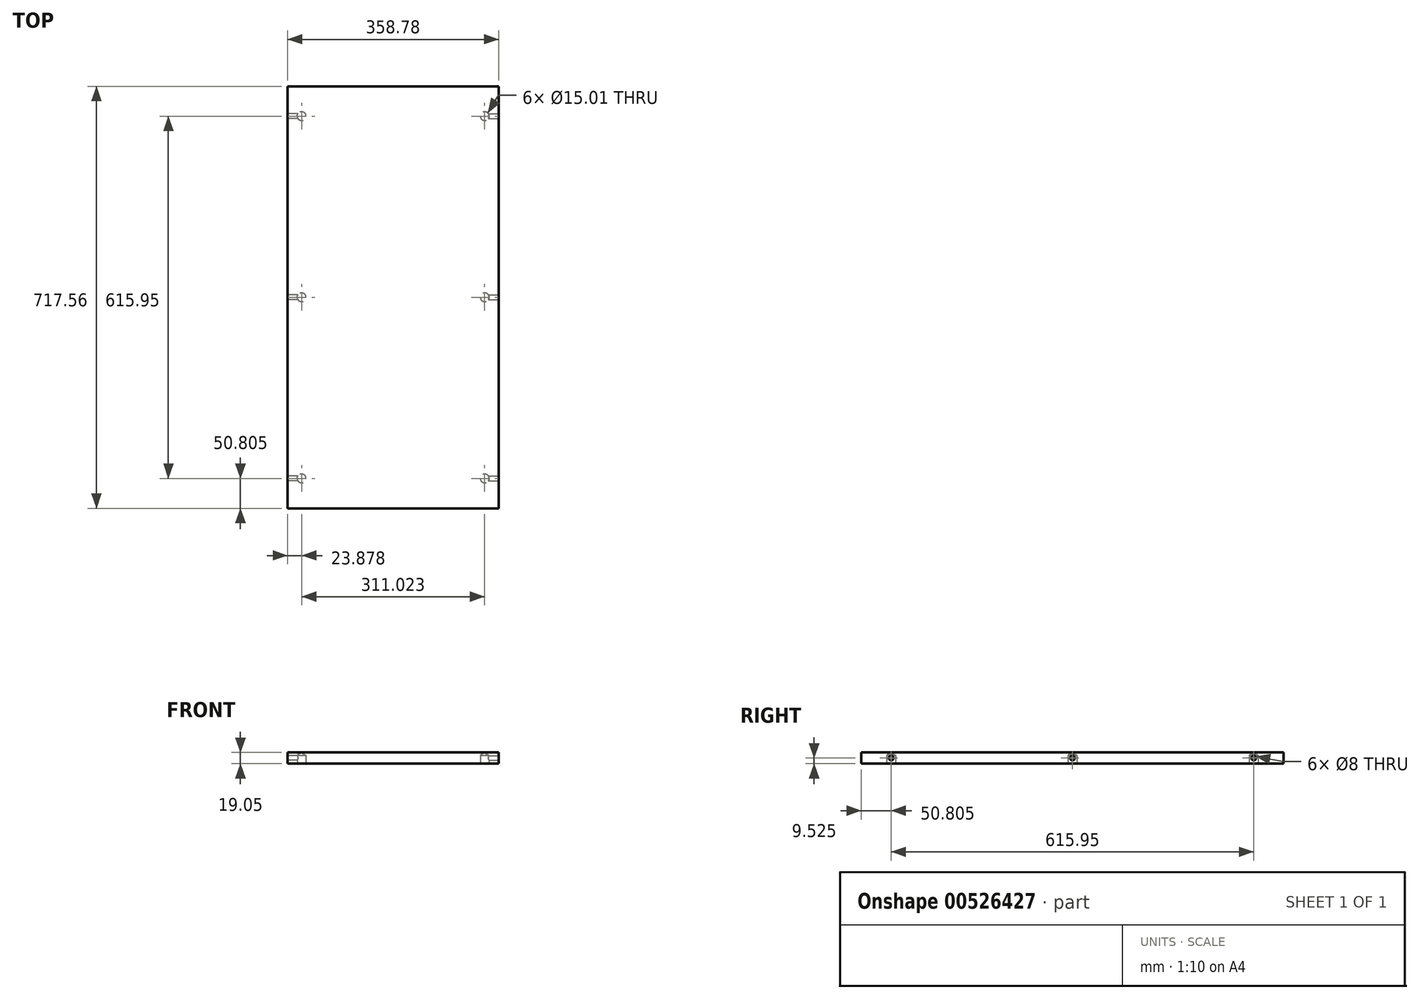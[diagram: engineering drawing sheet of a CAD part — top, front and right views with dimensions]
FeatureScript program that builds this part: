
annotation { "Feature Type Name" : "Feature", "Feature Type Description" : "" }
export const myFeature = defineFeature(function(context is Context, id is Id, definition is map)
    precondition{}
    {
        {
            var Q0;
            Q0=qCreatedBy(makeId("Top.planeOp"),FACE);
            var sketch = newSketch(context, id + "F0", { "sketchPlane" : qUnion([Q0])});
            skLineSegment(sketch, "E0.bottom", {"start": v(179.39, 358.78) * mm, "end": v(-179.39, 358.78) * mm});
            skLineSegment(sketch, "E0.top", {"start": v(179.39, -358.78) * mm, "end": v(-179.39, -358.78) * mm});
            skLineSegment(sketch, "E0.left", {"start": v(179.39, 358.77) * mm, "end": v(179.39, -358.78) * mm});
            skLineSegment(sketch, "E0.right", {"start": v(-179.39, 358.77) * mm, "end": v(-179.39, -358.78) * mm});
            skPoint(sketch, "E0.middle", {"position": v(0, 0) * mm});
            skSolve(sketch);
        }
        {
            var Q0;
            Q0=makeQuery(id+"F0.imprint","IMPRINT",FACE,{"disambiguationData":[TD([[makeQuery(id+"F0.imprint","IMPRINT",EDGE,{"derivedFrom":sQuery(id+"F0.wireOp",EDGE,"E0.bottom")}),1.0]])]});
            extrude(context, id + "F1", {"entities" : qUnion([Q0]), "depth" : 19.05 * mm, "offsetDistance" : 25.4 * mm});
        }
        {
            var Q0;
            Q0=makeQuery(id+"F1.opExtrude","SWEPT_FACE",FACE,{"disambiguationData":[OSD([sQuery(id+"F0.wireOp",EDGE,"E0.left")])]});
            var sketch = newSketch(context, id + "F2", { "sketchPlane" : qUnion([Q0])});
            skPoint(sketch, "E1", {"position": v(-307.98, 9.53) * mm});
            skPoint(sketch, "E2", {"position": v(0, 9.53) * mm});
            skPoint(sketch, "E3", {"position": v(307.97, 9.53) * mm});
            skSolve(sketch);
        }
        {
            var Q0;
            Q0=sQuery(id+"F2.wireOp",VERTEX,"E1");
            var Q1;
            Q1=sQuery(id+"F2.wireOp",VERTEX,"E2");
            var Q2;
            Q2=sQuery(id+"F2.wireOp",VERTEX,"E3");
            var Q3;
            Q3=makeQuery(id+"F1.opExtrude","SWEPT_BODY",BODY,{"disambiguationData":[OSD([sQuery(id+"F0.wireOp",EDGE,"E0.bottom"),sQuery(id+"F0.wireOp",EDGE,"E0.top"),sQuery(id+"F0.wireOp",EDGE,"E0.left"),sQuery(id+"F0.wireOp",EDGE,"E0.right")])]});
            hole(context, id + "F3", {"style" : HoleStyle.SIMPLE, "endStyle" : HoleEndStyle.BLIND, "holeDiameter" : 8 * mm, "holeDepth" : 25.4 * mm, "isTappedThrough" : true, "tappedDepth" : 12.7 * mm, "tapClearance" : 3, "startFromSketch" : true, "locations" : qUnion([Q0, Q1, Q2]), "scope" : qUnion([Q3])});
        }
        {
            var Q0;
            Q0=makeQuery(id+"F1.opExtrude","SWEPT_FACE",FACE,{"disambiguationData":[OSD([sQuery(id+"F0.wireOp",EDGE,"E0.right")])]});
            var sketch = newSketch(context, id + "F4", { "sketchPlane" : qUnion([Q0])});
            skPoint(sketch, "E4", {"position": v(0, 9.53) * mm});
            skPoint(sketch, "E5", {"position": v(307.98, 9.53) * mm});
            skPoint(sketch, "E6", {"position": v(-307.98, 9.53) * mm});
            skSolve(sketch);
        }
        {
            var Q0;
            Q0=sQuery(id+"F4.wireOp",VERTEX,"E6");
            var Q1;
            Q1=sQuery(id+"F4.wireOp",VERTEX,"E4");
            var Q2;
            Q2=sQuery(id+"F4.wireOp",VERTEX,"E5");
            var Q3;
            Q3=makeQuery(id+"F1.opExtrude","SWEPT_BODY",BODY,{"disambiguationData":[OSD([sQuery(id+"F0.wireOp",EDGE,"E0.bottom"),sQuery(id+"F0.wireOp",EDGE,"E0.top"),sQuery(id+"F0.wireOp",EDGE,"E0.left"),sQuery(id+"F0.wireOp",EDGE,"E0.right")])]});
            hole(context, id + "F5", {"style" : HoleStyle.SIMPLE, "endStyle" : HoleEndStyle.BLIND, "holeDiameter" : 8 * mm, "holeDepth" : 25.4 * mm, "isTappedThrough" : true, "tappedDepth" : 12.7 * mm, "tapClearance" : 3, "startFromSketch" : true, "locations" : qUnion([Q0, Q1, Q2]), "scope" : qUnion([Q3])});
        }
        {
            var Q0;
            Q0=makeQuery(id+"F1.opExtrude","CAP_FACE",FACE,{"disambiguationData":[OSD([sQuery(id+"F0.wireOp",EDGE,"E0.bottom"),sQuery(id+"F0.wireOp",EDGE,"E0.top"),sQuery(id+"F0.wireOp",EDGE,"E0.left"),sQuery(id+"F0.wireOp",EDGE,"E0.right")])],"isStart":true});
            var sketch = newSketch(context, id + "F6", { "sketchPlane" : qUnion([Q0])});
            skLineSegment(sketch, "E7", {"start": v(-179.39, 358.78) * mm, "end": v(-155.51, 358.78) * mm});
            skPoint(sketch, "E8", {"position": v(-134.62, -334.9) * mm});
            skPoint(sketch, "E9", {"position": v(0, -334.9) * mm});
            skPoint(sketch, "E10", {"position": v(128.59, -334.9) * mm});
            skPoint(sketch, "E11", {"position": v(155.51, -307.98) * mm});
            skPoint(sketch, "E12", {"position": v(-155.51, -307.98) * mm});
            skPoint(sketch, "E13", {"position": v(-155.51, 307.97) * mm});
            skPoint(sketch, "E14", {"position": v(155.51, 307.97) * mm});
            skPoint(sketch, "E15", {"position": v(155.51, 0) * mm});
            skPoint(sketch, "E16", {"position": v(-155.51, 0) * mm});
            skSolve(sketch);
        }
        {
            var Q0;
            Q0=sQuery(id+"F6.wireOp",VERTEX,"E13");
            var Q1;
            Q1=sQuery(id+"F6.wireOp",VERTEX,"E14");
            var Q2;
            Q2=sQuery(id+"F6.wireOp",VERTEX,"E15");
            var Q3;
            Q3=sQuery(id+"F6.wireOp",VERTEX,"E16");
            var Q4;
            Q4=sQuery(id+"F6.wireOp",VERTEX,"E12");
            var Q5;
            Q5=sQuery(id+"F6.wireOp",VERTEX,"E11");
            var Q6;
            Q6=makeQuery(id+"F1.opExtrude","SWEPT_BODY",BODY,{"disambiguationData":[OSD([sQuery(id+"F0.wireOp",EDGE,"E0.bottom"),sQuery(id+"F0.wireOp",EDGE,"E0.top"),sQuery(id+"F0.wireOp",EDGE,"E0.left"),sQuery(id+"F0.wireOp",EDGE,"E0.right")])]});
            hole(context, id + "F7", {"style" : HoleStyle.SIMPLE, "endStyle" : HoleEndStyle.BLIND, "holeDiameter" : 15 * mm, "holeDepth" : 14.22 * mm, "isTappedThrough" : true, "tappedDepth" : 12.7 * mm, "tapClearance" : 3, "startFromSketch" : true, "locations" : qUnion([Q0, Q1, Q2, Q3, Q4, Q5]), "scope" : qUnion([Q6])});
        }
    });
